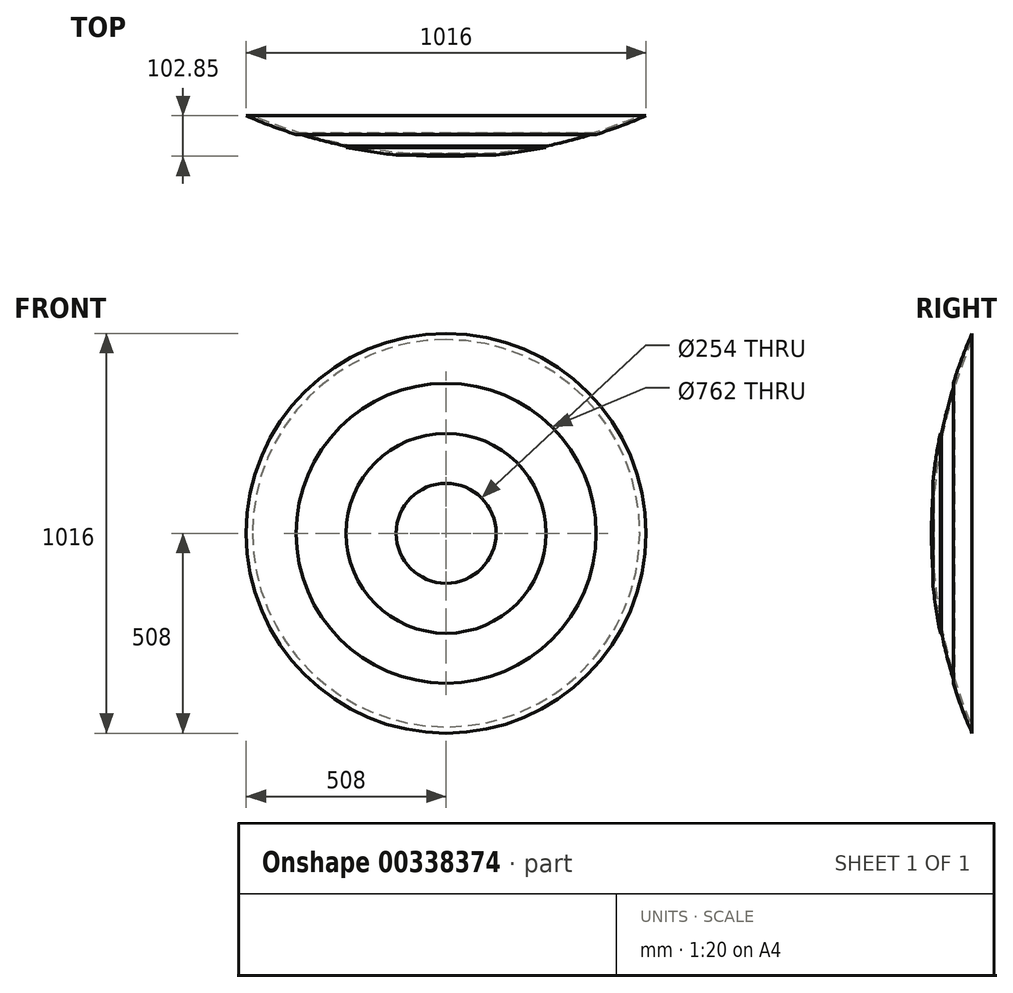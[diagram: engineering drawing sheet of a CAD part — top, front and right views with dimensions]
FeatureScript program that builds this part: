
annotation { "Feature Type Name" : "Feature", "Feature Type Description" : "" }
export const myFeature = defineFeature(function(context is Context, id is Id, definition is map)
    precondition{}
    {
        {
            var Q0;
            Q0=qCreatedBy(makeId("Top.planeOp"),FACE);
            var sketch = newSketch(context, id + "F0", { "sketchPlane" : qUnion([Q0])});
            skCircle(sketch, "E0", {"center": v(0, 0) * mm, "radius": 1270 * mm});
            skCircle(sketch, "E1", {"center": v(0, 0) * mm, "radius": 1263.65 * mm});
            skLineSegment(sketch, "E2", {"start": v(0, -1263.65) * mm, "end": v(0, -1270) * mm});
            skPoint(sketch, "E3", {"position": v(-508, -1254.35) * mm});
            skLineSegment(sketch, "E4", {"start": v(-508, -1254.35) * mm, "end": v(-508, -1163.97) * mm});
            skLineSegment(sketch, "E5", {"start": v(-508, -1163.97) * mm, "end": v(508, -1163.97) * mm});
            skPoint(sketch, "E6", {"position": v(-177.8, -1255.98) * mm});
            skPoint(sketch, "E7", {"position": v(-342.9, -1239.18) * mm});
            skPoint(sketch, "E8", {"position": v(254, -1256.25) * mm});
            skPoint(sketch, "E9", {"position": v(381, -1228.5) * mm});
            skPoint(sketch, "E10.start.orphan", {"position": v(0, -1266.83) * mm});
            skCircle(sketch, "E11", {"center": v(0, 0) * mm, "radius": 1266.83 * mm});
            skPoint(sketch, "E12.start.orphan", {"position": v(127, -1266.83) * mm});
            skLineSegment(sketch, "E13", {"start": v(381, -1228.5) * mm, "end": v(381, -1208.17) * mm});
            skLineSegment(sketch, "E14", {"start": v(254, -1256.25) * mm, "end": v(254, -1241.1) * mm});
            skLineSegment(sketch, "E15", {"start": v(127, -1266.83) * mm, "end": v(127, -1260.44) * mm});
            skSolve(sketch);
        }
        {
            var Q0;
            {var subQ1=sQuery(id+"F0.wireOp",EDGE,"E1");var subQ5=sQuery(id+"F0.wireOp",EDGE,"E2");var subQ6=makeQuery(id+"F0.imprint","INTERSECT",VERTEX,{"derivedFrom":[subQ1,subQ5]});Q0=makeQuery(id+"F0.imprint","IMPRINT",FACE,{"disambiguationData":[TD([[makeQuery(id+"F0.imprint","IMPRINT",EDGE,{"disambiguationData":[TD([[subQ6,-1.0]])],"derivedFrom":subQ1}),-1.0]])]});}
            var Q1;
            {var subQ0=sQuery(id+"F0.wireOp",EDGE,"E15");var subQ1=sQuery(id+"F0.wireOp",EDGE,"E0");var subQ2=makeQuery(id+"F0.imprint","INTERSECT",VERTEX,{"derivedFrom":[subQ1,subQ0]});Q1=makeQuery(id+"F0.imprint","IMPRINT",FACE,{"disambiguationData":[TD([[makeQuery(id+"F0.imprint","IMPRINT",EDGE,{"disambiguationData":[TD([[subQ2,-1.0]])],"derivedFrom":subQ1}),1.0]])]});}
            var Q2;
            {var subQ0=sQuery(id+"F0.wireOp",EDGE,"E5");var subQ1=sQuery(id+"F0.wireOp",EDGE,"E0");var subQ2=makeQuery(id+"F0.imprint","INTERSECT",VERTEX,{"disambiguationData":[OD(1.0)],"derivedFrom":[subQ1,subQ0]});Q2=makeQuery(id+"F0.imprint","IMPRINT",FACE,{"disambiguationData":[TD([[makeQuery(id+"F0.imprint","IMPRINT",EDGE,{"disambiguationData":[TD([[subQ2,1.0]])],"derivedFrom":subQ1}),1.0]])]});}
            var Q3;
            Q3=sQuery(id+"F0.wireOp",EDGE,"E2");
            revolve(context, id + "F1", {"entities" : qUnion([Q0, Q1, Q2]), "axis" : qUnion([Q3]), "revolveType" : RevolveType.FULL});
        }
    });
